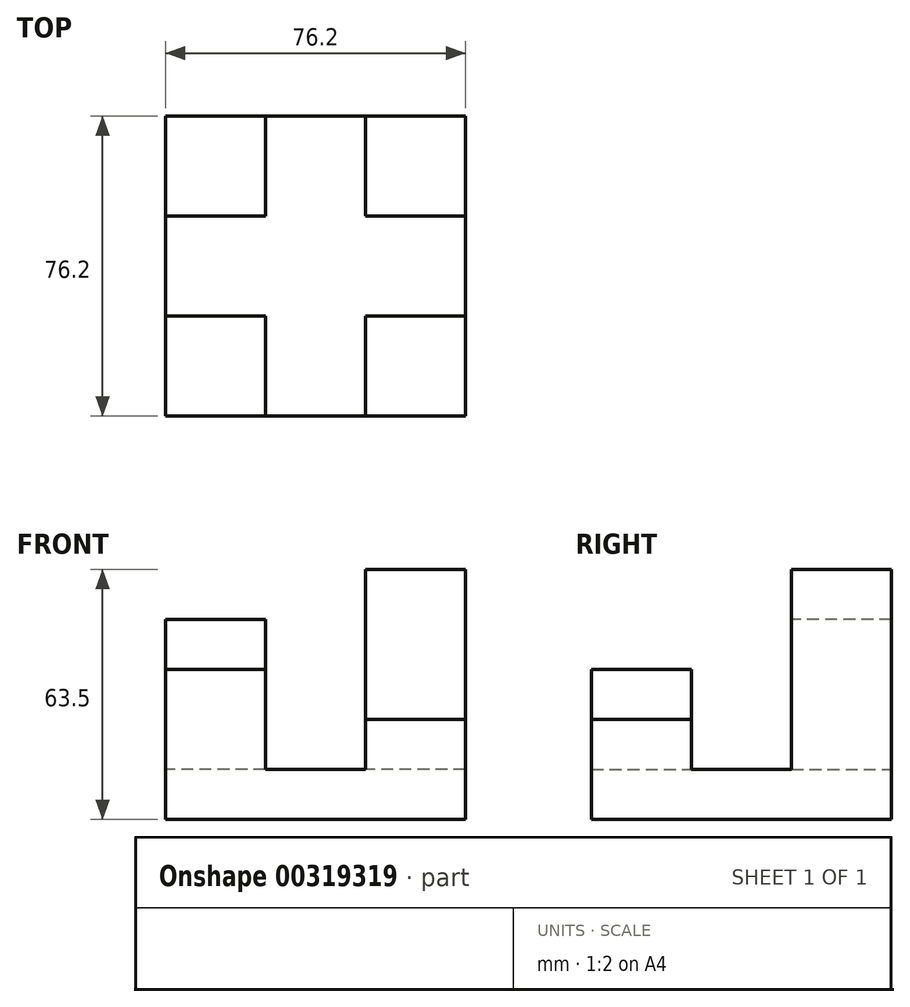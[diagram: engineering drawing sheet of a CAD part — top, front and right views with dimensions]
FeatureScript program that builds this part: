
annotation { "Feature Type Name" : "Feature", "Feature Type Description" : "" }
export const myFeature = defineFeature(function(context is Context, id is Id, definition is map)
    precondition{}
    {
        {
            var Q0;
            Q0=qCreatedBy(makeId("Top.planeOp"),FACE);
            var sketch = newSketch(context, id + "F0", { "sketchPlane" : qUnion([Q0])});
            skLineSegment(sketch, "E0", {"start": v(-28.66, -33.83) * mm, "end": v(47.54, -33.83) * mm});
            skLineSegment(sketch, "E1", {"start": v(47.54, -33.83) * mm, "end": v(47.54, 42.37) * mm});
            skLineSegment(sketch, "E2", {"start": v(47.54, 42.37) * mm, "end": v(-28.66, 42.37) * mm});
            skLineSegment(sketch, "E3", {"start": v(-28.66, 42.37) * mm, "end": v(-28.66, -33.83) * mm});
            skSolve(sketch);
        }
        {
            var Q0;
            Q0=makeQuery(id+"F0.imprint","IMPRINT",FACE,{"disambiguationData":[TD([[makeQuery(id+"F0.imprint","IMPRINT",EDGE,{"derivedFrom":sQuery(id+"F0.wireOp",EDGE,"E0")}),1.0]])]});
            extrude(context, id + "F1", {"entities" : qUnion([Q0]), "depth" : 12.7 * mm});
        }
        {
            var Q0;
            Q0=makeQuery(id+"F1.opExtrude","CAP_FACE",FACE,{"disambiguationData":[OSD([sQuery(id+"F0.wireOp",EDGE,"E0"),sQuery(id+"F0.wireOp",EDGE,"E1"),sQuery(id+"F0.wireOp",EDGE,"E2"),sQuery(id+"F0.wireOp",EDGE,"E3")])],"isStart":false});
            var sketch = newSketch(context, id + "F2", { "sketchPlane" : qUnion([Q0])});
            skLineSegment(sketch, "E4", {"start": v(47.54, -33.83) * mm, "end": v(22.14, -33.83) * mm});
            skLineSegment(sketch, "E5", {"start": v(22.14, -33.83) * mm, "end": v(22.14, -8.43) * mm});
            skLineSegment(sketch, "E6", {"start": v(22.14, -8.43) * mm, "end": v(47.54, -8.43) * mm});
            skLineSegment(sketch, "E7", {"start": v(47.54, -8.43) * mm, "end": v(47.54, -33.83) * mm});
            skSolve(sketch);
        }
        {
            var Q0;
            Q0=makeQuery(id+"F2.imprint","IMPRINT",FACE,{"disambiguationData":[TD([[makeQuery(id+"F2.imprint","IMPRINT",EDGE,{"derivedFrom":sQuery(id+"F2.wireOp",EDGE,"E4")}),1.0]])]});
            extrude(context, id + "F3", {"entities" : qUnion([Q0]), "operationType" : NewBodyOperationType.ADD, "depth" : 12.7 * mm});
        }
        {
            var Q0;
            Q0=makeQuery(id+"F1.opExtrude","CAP_FACE",FACE,{"disambiguationData":[OSD([sQuery(id+"F0.wireOp",EDGE,"E0"),sQuery(id+"F0.wireOp",EDGE,"E1"),sQuery(id+"F0.wireOp",EDGE,"E2"),sQuery(id+"F0.wireOp",EDGE,"E3")])],"isStart":false});
            var sketch = newSketch(context, id + "F4", { "sketchPlane" : qUnion([Q0])});
            skLineSegment(sketch, "E8", {"start": v(-28.66, -33.83) * mm, "end": v(-3.26, -33.83) * mm});
            skLineSegment(sketch, "E9", {"start": v(-3.26, -33.83) * mm, "end": v(-3.26, -8.43) * mm});
            skLineSegment(sketch, "E10", {"start": v(-3.26, -8.43) * mm, "end": v(-28.66, -8.43) * mm});
            skLineSegment(sketch, "E11", {"start": v(-28.66, -8.43) * mm, "end": v(-28.66, -33.83) * mm});
            skSolve(sketch);
        }
        {
            var Q0;
            Q0=makeQuery(id+"F4.imprint","IMPRINT",FACE,{"disambiguationData":[TD([[makeQuery(id+"F4.imprint","IMPRINT",EDGE,{"derivedFrom":sQuery(id+"F4.wireOp",EDGE,"E8")}),1.0]])]});
            extrude(context, id + "F5", {"entities" : qUnion([Q0]), "operationType" : NewBodyOperationType.ADD, "depth" : 25.4 * mm});
        }
        {
            var Q0;
            Q0=makeQuery(id+"F1.opExtrude","CAP_FACE",FACE,{"disambiguationData":[OSD([sQuery(id+"F0.wireOp",EDGE,"E0"),sQuery(id+"F0.wireOp",EDGE,"E1"),sQuery(id+"F0.wireOp",EDGE,"E2"),sQuery(id+"F0.wireOp",EDGE,"E3")])],"isStart":false});
            var sketch = newSketch(context, id + "F6", { "sketchPlane" : qUnion([Q0])});
            skLineSegment(sketch, "E12", {"start": v(-28.66, 42.37) * mm, "end": v(-3.26, 42.37) * mm});
            skLineSegment(sketch, "E13", {"start": v(-3.26, 42.37) * mm, "end": v(-3.26, 16.97) * mm});
            skLineSegment(sketch, "E14", {"start": v(-3.26, 16.97) * mm, "end": v(-28.66, 16.97) * mm});
            skLineSegment(sketch, "E15", {"start": v(-28.66, 16.97) * mm, "end": v(-28.66, 42.37) * mm});
            skSolve(sketch);
        }
        {
            var Q0;
            Q0=makeQuery(id+"F6.imprint","IMPRINT",FACE,{"disambiguationData":[TD([[makeQuery(id+"F6.imprint","IMPRINT",EDGE,{"derivedFrom":sQuery(id+"F6.wireOp",EDGE,"E12")}),1.0]])]});
            extrude(context, id + "F7", {"entities" : qUnion([Q0]), "operationType" : NewBodyOperationType.ADD, "depth" : 38.1 * mm});
        }
        {
            var Q0;
            Q0=makeQuery(id+"F1.opExtrude","CAP_FACE",FACE,{"disambiguationData":[OSD([sQuery(id+"F0.wireOp",EDGE,"E0"),sQuery(id+"F0.wireOp",EDGE,"E1"),sQuery(id+"F0.wireOp",EDGE,"E2"),sQuery(id+"F0.wireOp",EDGE,"E3")])],"isStart":false});
            var sketch = newSketch(context, id + "F8", { "sketchPlane" : qUnion([Q0])});
            skLineSegment(sketch, "E16", {"start": v(47.54, 16.97) * mm, "end": v(22.14, 16.97) * mm});
            skPoint(sketch, "E16.endSnap0", {"position": v(22.14, 42.37) * mm});
            skLineSegment(sketch, "E17", {"start": v(22.14, 16.97) * mm, "end": v(22.14, 42.37) * mm});
            skLineSegment(sketch, "E18", {"start": v(47.54, 42.37) * mm, "end": v(47.54, 16.97) * mm});
            skSolve(sketch);
        }
        {
            var Q0;
            Q0=makeQuery(id+"F8.imprint","IMPRINT",FACE,{"disambiguationData":[TD([[makeQuery(id+"F8.imprint","IMPRINT",EDGE,{"derivedFrom":sQuery(id+"F8.wireOp",EDGE,"E16")}),-1.0]])]});
            extrude(context, id + "F9", {"entities" : qUnion([Q0]), "operationType" : NewBodyOperationType.ADD, "depth" : 50.8 * mm});
        }
    });
